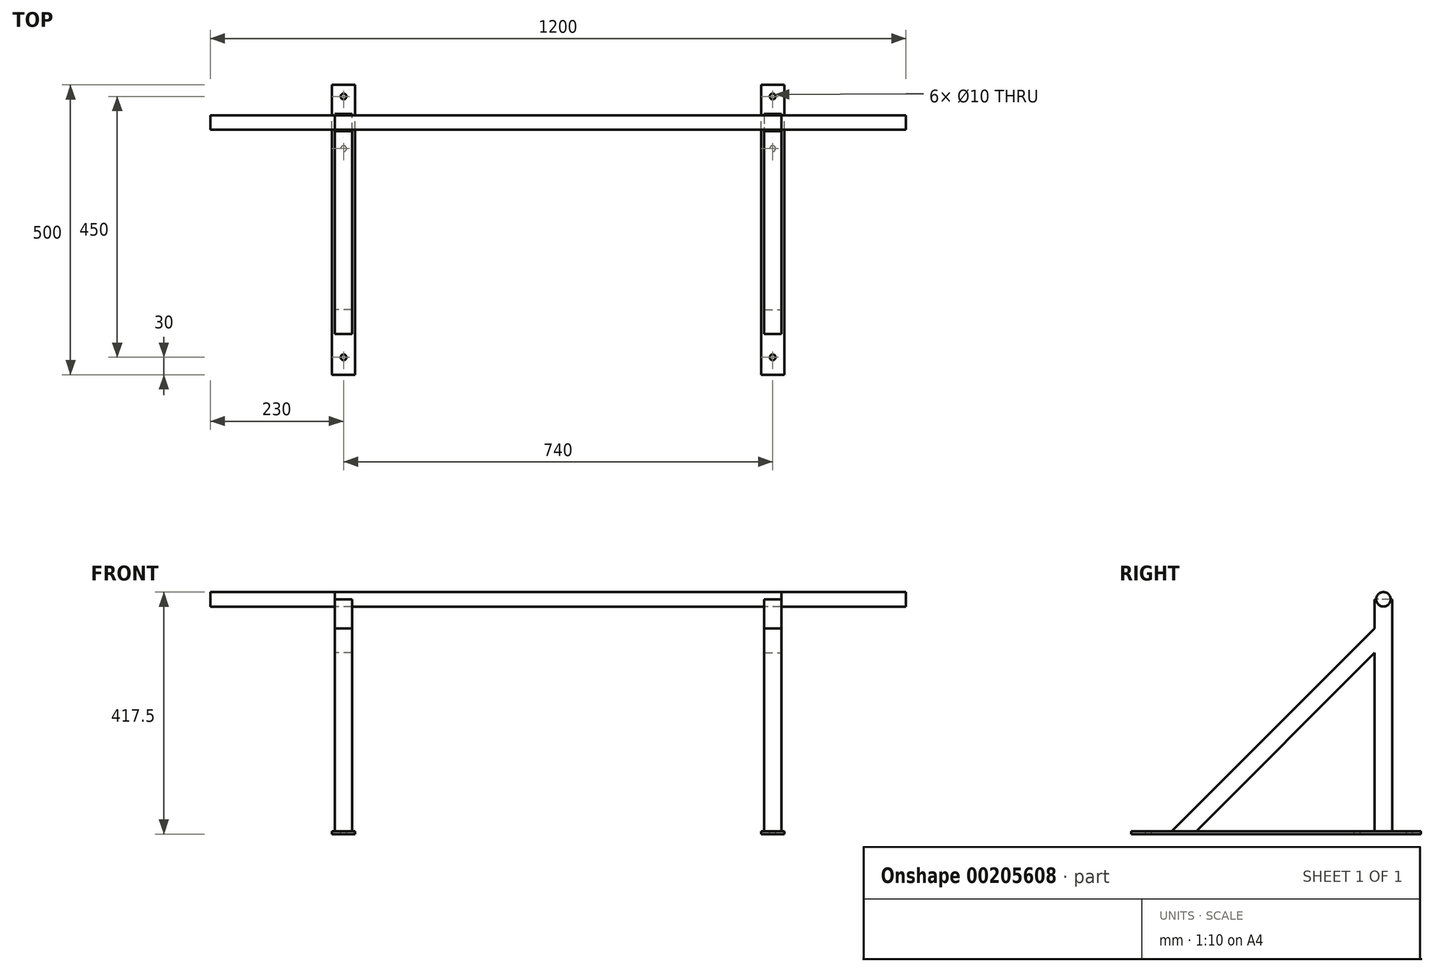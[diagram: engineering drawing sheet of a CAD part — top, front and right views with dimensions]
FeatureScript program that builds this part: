
annotation { "Feature Type Name" : "Feature", "Feature Type Description" : "" }
export const myFeature = defineFeature(function(context is Context, id is Id, definition is map)
    precondition{}
    {
        {
            var Q0;
            Q0=qCreatedBy(makeId("Top.planeOp"),FACE);
            var sketch = newSketch(context, id + "F0", { "sketchPlane" : qUnion([Q0])});
            skLineSegment(sketch, "E0.bottom", {"start": v(-350, -250) * mm, "end": v(-390, -250) * mm});
            skLineSegment(sketch, "E0.top", {"start": v(-350, 250) * mm, "end": v(-390, 250) * mm});
            skLineSegment(sketch, "E0.left", {"start": v(-350, -250) * mm, "end": v(-350, 250) * mm});
            skLineSegment(sketch, "E0.right", {"start": v(-390, -250) * mm, "end": v(-390, 250) * mm});
            skPoint(sketch, "E0.middle", {"position": v(-370, 0) * mm});
            skLineSegment(sketch, "E1.bottom", {"start": v(350, -250) * mm, "end": v(390, -250) * mm});
            skLineSegment(sketch, "E1.top", {"start": v(350, 250) * mm, "end": v(390, 250) * mm});
            skLineSegment(sketch, "E1.left", {"start": v(350, -250) * mm, "end": v(350, 250) * mm});
            skLineSegment(sketch, "E1.right", {"start": v(390, -250) * mm, "end": v(390, 250) * mm});
            skPoint(sketch, "E1.middle", {"position": v(370, 0) * mm});
            skSolve(sketch);
        }
        {
            var Q0;
            Q0 = qSketchRegion(id + "F0", true);
            extrude(context, id + "F1", {"entities" : qUnion([Q0]), "depth" : 5 * mm});
        }
        {
            var Q0;
            Q0=makeQuery(id+"F1.opExtrude","CAP_FACE",FACE,{"disambiguationData":[OSD([sQuery(id+"F0.wireOp",EDGE,"E0.bottom"),sQuery(id+"F0.wireOp",EDGE,"E0.top"),sQuery(id+"F0.wireOp",EDGE,"E0.left"),sQuery(id+"F0.wireOp",EDGE,"E0.right")])],"isStart":false});
            var sketch = newSketch(context, id + "F2", { "sketchPlane" : qUnion([Q0])});
            skLineSegment(sketch, "E2.bottom", {"start": v(-355, 170) * mm, "end": v(-385, 170) * mm});
            skLineSegment(sketch, "E2.top", {"start": v(-355, 200) * mm, "end": v(-385, 200) * mm});
            skLineSegment(sketch, "E2.left", {"start": v(-355, 170) * mm, "end": v(-355, 200) * mm});
            skLineSegment(sketch, "E2.right", {"start": v(-385, 170) * mm, "end": v(-385, 200) * mm});
            skPoint(sketch, "E2.middle", {"position": v(-370, 185) * mm});
            skPoint(sketch, "E2.middle.positionSnap0", {"position": v(-370, 250) * mm});
            skPoint(sketch, "E2.centerSnap0", {"position": v(-370, 250) * mm});
            skCircle(sketch, "E3", {"center": v(-370, 230) * mm, "radius": 5 * mm});
            skCircle(sketch, "E4", {"center": v(-370, 140) * mm, "radius": 5 * mm});
            skPoint(sketch, "E4.centerSnap0", {"position": v(-370, 170) * mm});
            skCircle(sketch, "E5", {"center": v(-370, -220) * mm, "radius": 5 * mm});
            skPoint(sketch, "E5.centerSnap0", {"position": v(-370, -250) * mm});
            skSolve(sketch);
        }
        {
            var Q0;
            Q0=makeQuery(id+"F2.imprint","IMPRINT",FACE,{"disambiguationData":[TD([[makeQuery(id+"F2.imprint","IMPRINT",EDGE,{"derivedFrom":sQuery(id+"F2.wireOp",EDGE,"E2.bottom")}),-1.0]])]});
            extrude(context, id + "F3", {"entities" : qUnion([Q0]), "operationType" : NewBodyOperationType.ADD, "depth" : 400 * mm});
        }
        {
            var Q0;
            Q0=makeQuery(id+"F1.opExtrude","CAP_FACE",FACE,{"disambiguationData":[OSD([sQuery(id+"F0.wireOp",EDGE,"E1.bottom"),sQuery(id+"F0.wireOp",EDGE,"E1.top"),sQuery(id+"F0.wireOp",EDGE,"E1.left"),sQuery(id+"F0.wireOp",EDGE,"E1.right")])],"isStart":false});
            var sketch = newSketch(context, id + "F4", { "sketchPlane" : qUnion([Q0])});
            skLineSegment(sketch, "E6.bottom", {"start": v(385, 200) * mm, "end": v(355, 200) * mm});
            skLineSegment(sketch, "E6.top", {"start": v(385, 170) * mm, "end": v(355, 170) * mm});
            skLineSegment(sketch, "E6.left", {"start": v(385, 200) * mm, "end": v(385, 170) * mm});
            skLineSegment(sketch, "E6.right", {"start": v(355, 200) * mm, "end": v(355, 170) * mm});
            skPoint(sketch, "E6.middle", {"position": v(370, 185) * mm});
            skPoint(sketch, "E6.middle.positionSnap0", {"position": v(370, 250) * mm});
            skPoint(sketch, "E6.centerSnap0", {"position": v(370, 250) * mm});
            skCircle(sketch, "E7", {"center": v(370, 230) * mm, "radius": 5 * mm});
            skCircle(sketch, "E8", {"center": v(370, 140) * mm, "radius": 5 * mm});
            skCircle(sketch, "E9", {"center": v(370, -220) * mm, "radius": 5 * mm});
            skPoint(sketch, "E9.centerSnap0", {"position": v(370, -250) * mm});
            skSolve(sketch);
        }
        {
            var Q0;
            Q0=makeQuery(id+"F4.imprint","IMPRINT",FACE,{"disambiguationData":[TD([[makeQuery(id+"F4.imprint","IMPRINT",EDGE,{"derivedFrom":sQuery(id+"F4.wireOp",EDGE,"E7")}),1.0]])]});
            var Q1;
            Q1=makeQuery(id+"F4.imprint","IMPRINT",FACE,{"disambiguationData":[TD([[makeQuery(id+"F4.imprint","IMPRINT",EDGE,{"derivedFrom":sQuery(id+"F4.wireOp",EDGE,"E8")}),1.0]])]});
            var Q2;
            Q2=makeQuery(id+"F4.imprint","IMPRINT",FACE,{"disambiguationData":[TD([[makeQuery(id+"F4.imprint","IMPRINT",EDGE,{"derivedFrom":sQuery(id+"F4.wireOp",EDGE,"E9")}),1.0]])]});
            extrude(context, id + "F5", {"entities" : qUnion([Q0, Q1, Q2]), "operationType" : NewBodyOperationType.REMOVE, "oppositeDirection" : true, "depth" : 25 * mm});
        }
        {
            var Q0;
            Q0=makeQuery(id+"F4.imprint","IMPRINT",FACE,{"disambiguationData":[TD([[makeQuery(id+"F4.imprint","IMPRINT",EDGE,{"derivedFrom":sQuery(id+"F4.wireOp",EDGE,"E6.bottom")}),1.0]])]});
            extrude(context, id + "F6", {"entities" : qUnion([Q0]), "operationType" : NewBodyOperationType.ADD, "depth" : 400 * mm});
        }
        {
            var Q0;
            Q0=makeQuery(id+"F2.imprint","IMPRINT",FACE,{"disambiguationData":[TD([[makeQuery(id+"F2.imprint","IMPRINT",EDGE,{"derivedFrom":sQuery(id+"F2.wireOp",EDGE,"E4")}),1.0]])]});
            var Q1;
            Q1=makeQuery(id+"F2.imprint","IMPRINT",FACE,{"disambiguationData":[TD([[makeQuery(id+"F2.imprint","IMPRINT",EDGE,{"derivedFrom":sQuery(id+"F2.wireOp",EDGE,"E3")}),1.0]])]});
            var Q2;
            Q2=makeQuery(id+"F2.imprint","IMPRINT",FACE,{"disambiguationData":[TD([[makeQuery(id+"F2.imprint","IMPRINT",EDGE,{"derivedFrom":sQuery(id+"F2.wireOp",EDGE,"E5")}),1.0]])]});
            extrude(context, id + "F7", {"entities" : qUnion([Q0, Q1, Q2]), "operationType" : NewBodyOperationType.REMOVE, "oppositeDirection" : true, "depth" : 25 * mm});
        }
        {
            var Q0;
            Q0=makeQuery(id+"F3.opExtrude","SWEPT_FACE",FACE,{"disambiguationData":[OSD([sQuery(id+"F2.wireOp",EDGE,"E2.right")])]});
            var sketch = newSketch(context, id + "F8", { "sketchPlane" : qUnion([Q0])});
            skLineSegment(sketch, "E10", {"start": v(-170, 312.57) * mm, "end": v(137.57, 5) * mm});
            skLineSegment(sketch, "E11", {"start": v(137.57, 5) * mm, "end": v(180, 5) * mm});
            skLineSegment(sketch, "E12", {"start": v(180, 5) * mm, "end": v(-170, 355) * mm});
            skLineSegment(sketch, "E13", {"start": v(-170, 355) * mm, "end": v(-170, 312.57) * mm});
            skSolve(sketch);
        }
        {
            var Q0;
            Q0 = qSketchRegion(id + "F8", true);
            extrude(context, id + "F9", {"entities" : qUnion([Q0]), "operationType" : NewBodyOperationType.ADD, "oppositeDirection" : true, "depth" : 30 * mm});
        }
        {
            var Q0;
            Q0=makeQuery(id+"F6.opExtrude","SWEPT_FACE",FACE,{"disambiguationData":[OSD([sQuery(id+"F4.wireOp",EDGE,"E6.left")])]});
            var sketch = newSketch(context, id + "F10", { "sketchPlane" : qUnion([Q0])});
            skLineSegment(sketch, "E14", {"start": v(170, 312.57) * mm, "end": v(-137.57, 5) * mm});
            skLineSegment(sketch, "E15", {"start": v(-137.57, 5) * mm, "end": v(-180, 5) * mm});
            skLineSegment(sketch, "E16", {"start": v(-180, 5) * mm, "end": v(170, 355) * mm});
            skLineSegment(sketch, "E17", {"start": v(170, 355) * mm, "end": v(170, 312.57) * mm});
            skSolve(sketch);
        }
        {
            var Q0;
            Q0 = qSketchRegion(id + "F10", true);
            extrude(context, id + "F11", {"entities" : qUnion([Q0]), "operationType" : NewBodyOperationType.ADD, "oppositeDirection" : true, "depth" : 30 * mm});
        }
        {
            var Q0;
            Q0=makeQuery(id+"F9.boolean.opBoolean","MERGE",FACE,{"derivedFrom":[makeQuery(id+"F3.opExtrude","SWEPT_FACE",FACE,{"disambiguationData":[OSD([sQuery(id+"F2.wireOp",EDGE,"E2.right")])]}),makeQuery(id+"F9.opExtrude","CAP_FACE",FACE,{"disambiguationData":[OSD([sQuery(id+"F8.wireOp",EDGE,"E10"),sQuery(id+"F8.wireOp",EDGE,"E11"),sQuery(id+"F8.wireOp",EDGE,"E12"),sQuery(id+"F8.wireOp",EDGE,"E13")])],"isStart":true})]});
            var sketch = newSketch(context, id + "F12", { "sketchPlane" : qUnion([Q0])});
            skCircle(sketch, "E18", {"center": v(-185, 405) * mm, "radius": 12.5 * mm});
            skPoint(sketch, "E18.centerSnap0", {"position": v(-185, 405) * mm});
            skSolve(sketch);
        }
        {
            var Q0;
            Q0 = qSketchRegion(id + "F12", true);
            extrude(context, id + "F13", {"entities" : qUnion([Q0]), "oppositeDirection" : true, "depth" : (700 + 30 + 30 + 10) * mm});
        }
        {
            var Q0;
            Q0=makeQuery(id+"F13.opExtrude","CAP_FACE",FACE,{"disambiguationData":[OSD([sQuery(id+"F12.wireOp",EDGE,"E18")])],"isStart":false});
            extrude(context, id + "F14", {"entities" : qUnion([Q0]), "depth" : 215 * mm});
        }
        {
            var Q0;
            Q0=makeQuery(id+"F13.opExtrude","CAP_FACE",FACE,{"disambiguationData":[OSD([sQuery(id+"F12.wireOp",EDGE,"E18")])],"isStart":true});
            extrude(context, id + "F15", {"entities" : qUnion([Q0]), "depth" : 215 * mm});
        }
    });
